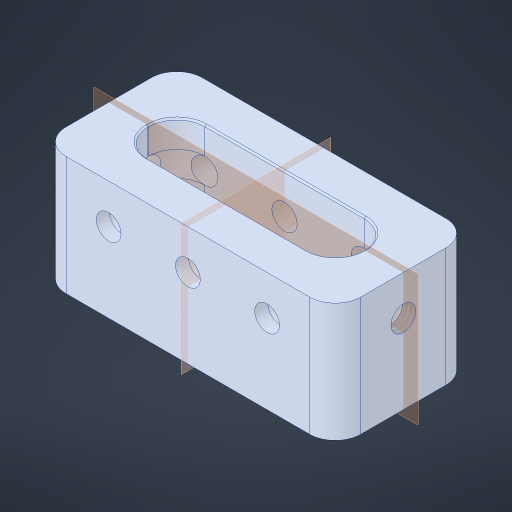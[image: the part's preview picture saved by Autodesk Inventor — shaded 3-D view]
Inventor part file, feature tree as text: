
AUTODESK INVENTOR PART (.ipt)
format: ipt  version: 2023.4 (Build 274418000, 418)  size: 473,088 bytes
history: native  units: in
note: dims shown in document units (in); Inventor stores cm internally (conversion verified against a paired STEP export)
features: sketch x4, hole x3, projected_geometry x2, extrude x1, chamfer x1
ambient origin geometry x8: Origin, YZ Plane, XZ Plane, XY Plane, X Axis, Y Axis, Z Axis, Center Point
bodies: Solid1 (feature_tree)
feature tree (11):
  extrude  "Extrusion1"  Depth=1.0in TaperAngle=0.0deg
  hole  "Hole1"  [1 undecoded]
  hole  "Hole2"  [1 undecoded]
  hole  "Hole3"  [1 undecoded]
  sketch  "Sketch1"  dims[d0=0.0625in d1=1.0in d2=0.0in]
  projected_geometry  "Projected Loop1"
  sketch  "Sketch2"  dims[d3=0.156in d4=0.38in d5=0.385in d6=0.25in d7=0.563in d8=1.0in d9=0.8108in]
  projected_geometry  "Projected Loop2"
  sketch  "Sketch3"  dims[d10=0.196in d11=0.5in d12=0.375in d13=0.25in d14=0.5635in d15=1.0in d16=0.8108in]
  sketch  "Sketch4"  dims[d17=0.156in d18=0.38in d19=0.385in d20=0.25in d21=0.563in d22=1.0in d23=0.8108in]
  chamfer  "Chamfer2"  [1 undecoded]
note: 4 required parameter values undecoded (feature->parameter linkage not recoverable at this tier; creation-order binding heuristic only, values carry confidence <= 0.55)
